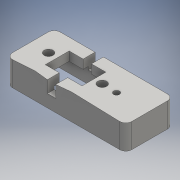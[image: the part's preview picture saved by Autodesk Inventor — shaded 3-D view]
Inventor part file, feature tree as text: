
AUTODESK INVENTOR PART (.ipt)
format: ipt  version: 2016 SP1 (Build 200210100, 210)  size: 196,096 bytes
history: native  units: mm
features: sketch x5, extrude x5, reference x2, plane x1
ambient origin geometry x8: Origin, YZ Plane, XZ Plane, XY Plane, X Axis, Y Axis, Z Axis, Center Point
bodies: Solid1 (feature_tree)
feature tree (13):
  plane  "Work Plane1"
  sketch  "Sketch1"  dims[d2=6.0mm d3=12.684184mm]
  extrude  "Extrusion4"  Depth=12.684184mm
  extrude  "Extrusion5"  Depth=2.0mm
  extrude  "Extrusion6"  Depth=5.2mm
  extrude  "Extrusion7"  Depth=3.0mm TaperAngle=0.0deg
  extrude  "Extrusion8"  Depth=4.0mm
  sketch  "Sketch5"  dims[d4=2.0mm d5=7.0mm]
  reference  "Reference11"
  reference  "Reference12"
  sketch  "Sketch6"  dims[d14=5.2mm d15=0.0mm d16=6.0mm]
  sketch  "Sketch7"  dims[d17=7.0mm d18=3.0mm d19=0.0mm]
  sketch  "Sketch8"  dims[d20=4.0mm d21=0.0mm d22=4.0mm d23=4.0mm d24=0.7mm d25=5.2mm d26=0.0mm d27=2.0mm d28=5.0mm d29=4.0mm d30=0.0mm d31=1.5mm]
